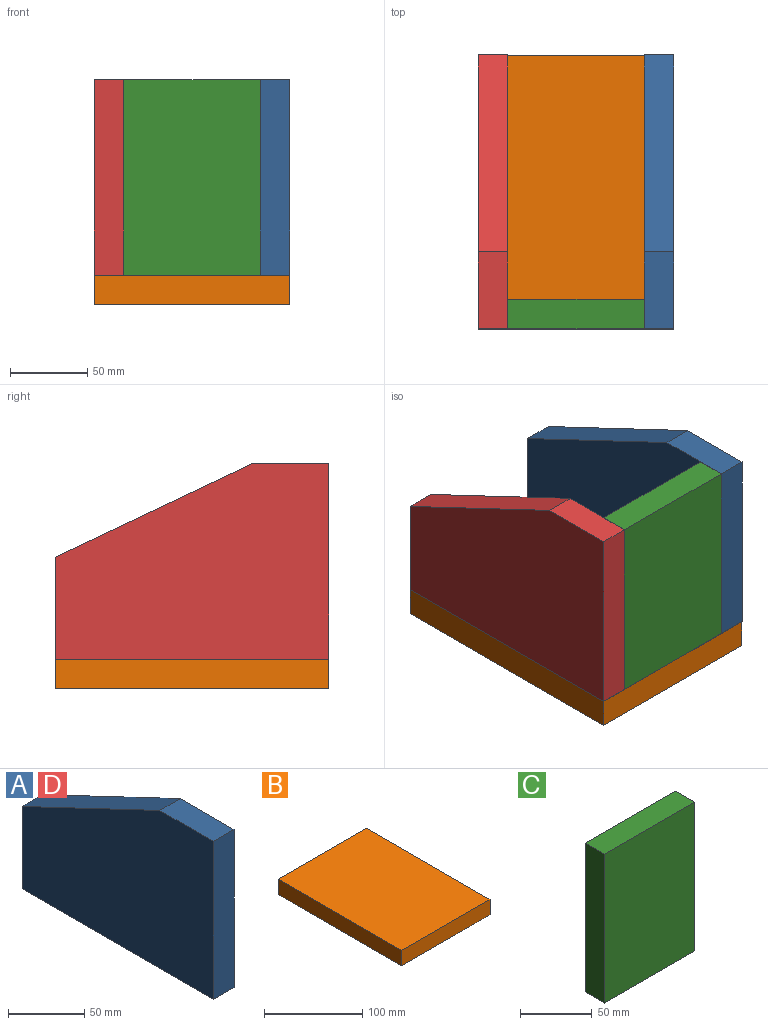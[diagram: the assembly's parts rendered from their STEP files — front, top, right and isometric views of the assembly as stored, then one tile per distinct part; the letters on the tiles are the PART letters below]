
ASSEMBLY  parts=4 mates=9
PART A: 7 faces, bbox 19.1x177.8x127 mm
  f0: plane 66.23x19.05mm, normal (0,1,0), area 1261.6mm2, adj f1,f4,f5,f6
  f1: plane 177.8x127mm, normal (1,0,0), area 18692.4mm2, adj f0,f2,f3,f4,f6
  f2: plane 49.84x19.05mm, normal (0,0,1), area 949.5mm2, adj f1,f3,f5,f6
  f3: plane 127x19.05mm, normal (0,-1,0), area 2419.3mm2, adj f1,f2,f4,f5
  f4: plane 177.8x19.05mm, normal (0,0,-1), area 3387.1mm2, adj f0,f1,f3,f5
  f5: plane 177.8x127mm, normal (-1,0,0), area 18692.4mm2, adj f0,f2,f3,f4,f6
  f6: plane 127.96x60.77mm, normal (0,0.43,0.9), area 2698.6mm2, adj f0,f1,f2,f5
PART B: 6 faces, bbox 127x177.8x19.1 mm
  f0: plane 127x19.05mm, normal (0,1,0), area 2419.3mm2, adj f1,f3,f4,f5
  f1: plane 177.8x19.05mm, normal (-1,0,0), area 3387.1mm2, adj f0,f2,f4,f5
  f2: plane 127x19.05mm, normal (0,-1,0), area 2419.3mm2, adj f1,f3,f4,f5
  f3: plane 177.8x19.05mm, normal (1,0,0), area 3387.1mm2, adj f0,f2,f4,f5
  f4: plane 177.8x127mm, normal (0,0,1), area 22580.6mm2, adj f0,f1,f2,f3
  f5: plane 177.8x127mm, normal (0,0,-1), area 22580.6mm2, adj f0,f1,f2,f3
PART C: 6 faces, bbox 88.9x19.1x127 mm
  f0: plane 127x19.05mm, normal (-1,0,0), area 2419.3mm2, adj f1,f3,f4,f5
  f1: plane 88.9x19.05mm, normal (0,0,-1), area 1693.5mm2, adj f0,f2,f4,f5
  f2: plane 127x19.05mm, normal (1,0,0), area 2419.3mm2, adj f1,f3,f4,f5
  f3: plane 88.9x19.05mm, normal (0,0,1), area 1693.5mm2, adj f0,f2,f4,f5
  f4: plane 127x88.9mm, normal (0,-1,0), area 11290.3mm2, adj f0,f1,f2,f3
  f5: plane 127x88.9mm, normal (0,1,0), area 11290.3mm2, adj f0,f1,f2,f3
PART D: same geometry as A
PLACE A t=(78.74,69.49,-94.54)mm
PLACE B t=(-29.21,-11.83,-81.85)mm
PLACE C t=(97.47,7.22,-21.44)mm
PLACE D t=(-29.21,69.49,-94.54)mm
MATE planar D.f3 <-> B.f2  axis (0,-1,0) through (-19.69,-11.83,0.7)mm
MATE planar D.f5 <-> B.f1  axis (-1,0,0) through (-29.21,67.45,-8.29)mm
MATE planar C.f4 <-> B.f2  axis (0,-1,0) through (34.29,-11.83,0.7)mm
MATE planar A.f0 <-> B.f0  axis (0,1,0) through (88.26,165.97,-29.68)mm
MATE planar A.f4 <-> B.f4  axis (0,0,-1) through (88.26,77.07,-62.8)mm
MATE planar C.f2 <-> A.f5  axis (1,0,0) through (78.74,-2.31,0.7)mm
MATE planar A.f1 <-> B.f3  axis (1,0,0) through (97.79,67.45,-8.29)mm
MATE planar D.f4 <-> B.f4  axis (0,0,-1) through (-19.69,77.07,-62.8)mm
MATE planar C.f1 <-> B.f4  axis (0,0,-1) through (34.29,-2.31,-62.8)mm
